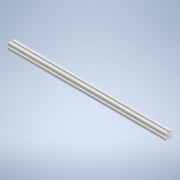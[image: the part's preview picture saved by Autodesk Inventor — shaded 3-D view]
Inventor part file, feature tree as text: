
AUTODESK INVENTOR PART (.ipt)
format: ipt  version: 2020.2 (Build 242310000, 310)  size: 177,664 bytes
history: native  units: in
note: dims shown in document units (in); Inventor stores cm internally (conversion verified against a paired STEP export)
features: extrude x1, sketch x1
ambient origin geometry x8: Origin, YZ Plane, XZ Plane, XY Plane, X Axis, Y Axis, Z Axis, Center Point
bodies: Solid1 (feature_tree)
feature tree (2):
  extrude  "Extrusion1"  Depth=0.29in
  sketch  "Sketch2"  dims[d9=0.2325in d18=0.055in d20=0.055in d34=0.29in d35=0.055in d37=0.058in d38=0.1225in d39=0.081in d40=135.0deg d41=0.17in d42=0.081in d43=0.058in d44=0.055in d45=0.75in d46=0.055in d47=1.5748in d49=360.0deg d51=0.2348in d52=0.232in d56=0.75in d58=0.125in d61=0.055in d62=0.055in d63=0.055in d64=0.055in d65=1.5748in d67=360.0deg d69=18.0in d70=0.0in d71=0.1225in]
